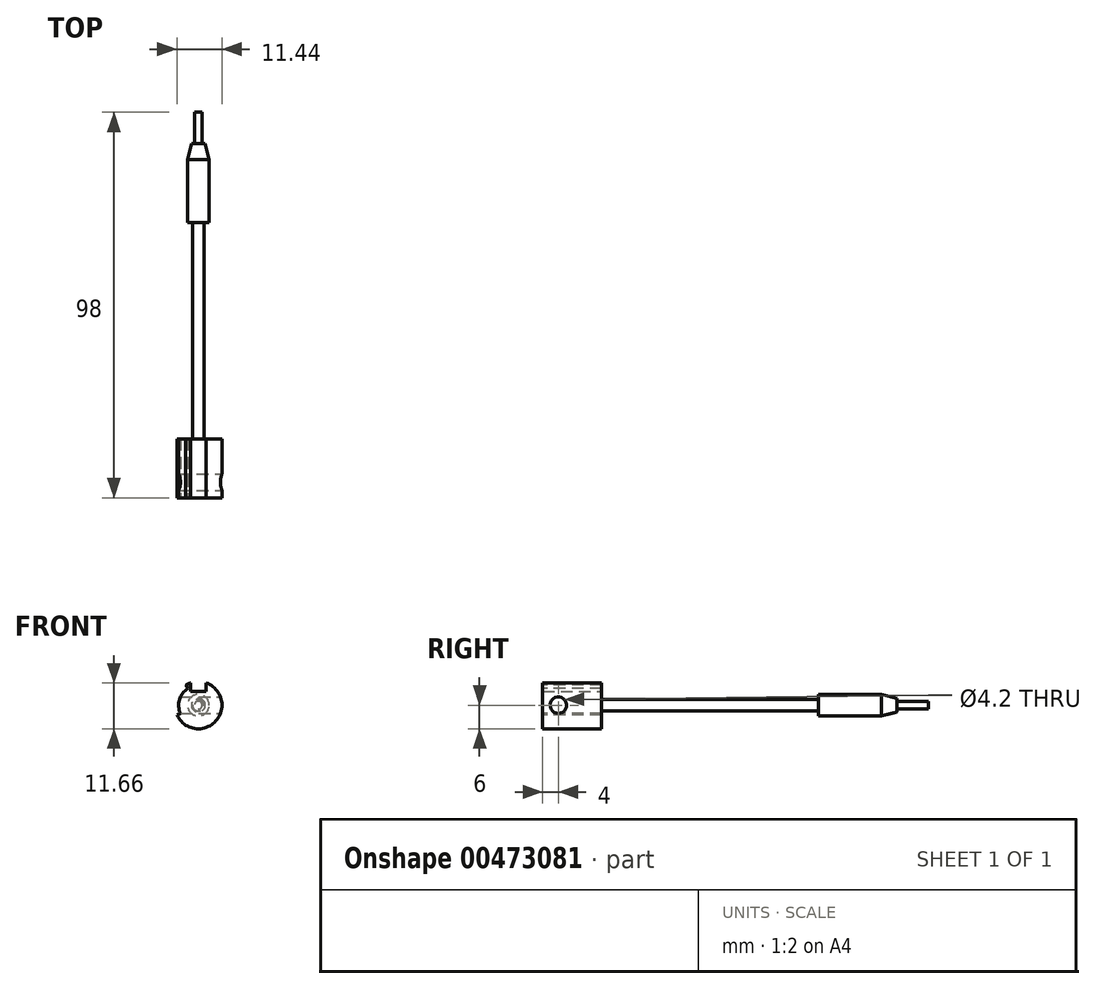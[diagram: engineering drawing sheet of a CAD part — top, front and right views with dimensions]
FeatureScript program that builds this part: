
annotation { "Feature Type Name" : "Feature", "Feature Type Description" : "" }
export const myFeature = defineFeature(function(context is Context, id is Id, definition is map)
    precondition{}
    {
        {
            var Q0;
            Q0=qCreatedBy(makeId("Front.planeOp"),FACE);
            var sketch = newSketch(context, id + "F0", { "sketchPlane" : qUnion([Q0])});
            skCircle(sketch, "E0", {"center": v(0, 0) * mm, "radius": 1 * mm});
            skSolve(sketch);
        }
        {
            var Q0;
            Q0=qSketchRegion(id+"F0",true);
            extrude(context, id + "F1", {"entities" : qUnion([Q0]), "oppositeDirection" : true, "depth" : 8 * mm});
        }
        {
            var Q0;
            Q0=makeQuery(id+"F1.opExtrude","CAP_FACE",FACE,{"disambiguationData":[OSD([sQuery(id+"F0.wireOp",EDGE,"E0")])],"isStart":true});
            var sketch = newSketch(context, id + "F2", { "sketchPlane" : qUnion([Q0])});
            skCircle(sketch, "E1", {"center": v(0, 0) * mm, "radius": 2.75 * mm});
            skSolve(sketch);
        }
        {
            var Q0;
            Q0=qSketchRegion(id+"F2",true);
            extrude(context, id + "F3", {"entities" : qUnion([Q0]), "operationType" : NewBodyOperationType.ADD, "depth" : 80 * mm});
        }
        {
            var Q0;
            Q0=makeQuery(id+"F3.opExtrude","CAP_EDGE",EDGE,{"disambiguationData":[OSD([sQuery(id+"F2.wireOp",EDGE,"E1")])],"isStart":true});
            chamfer(context, id + "F4", {"entities" : qUnion([Q0]), "chamferType" : ChamferType.TWO_OFFSETS, "width1" : 4 * mm, "oppositeDirection" : false, "width2" : 1 * mm, "tangentPropagation" : true});
        }
        {
            var Q0;
            Q0=makeQuery(id+"F3.opExtrude","CAP_FACE",FACE,{"disambiguationData":[OSD([sQuery(id+"F2.wireOp",EDGE,"E1")])],"isStart":false});
            var sketch = newSketch(context, id + "F5", { "sketchPlane" : qUnion([Q0])});
            skCircle(sketch, "E2", {"center": v(0, 0) * mm, "radius": 6 * mm});
            skSolve(sketch);
        }
        {
            var Q0;
            Q0=makeQuery(id+"F5.imprint","IMPRINT",FACE,{"disambiguationData":[TD([[makeQuery(id+"F5.imprint","IMPRINT",EDGE,{"derivedFrom":sQuery(id+"F5.wireOp",EDGE,"E2")}),1.0]])]});
            extrude(context, id + "F6", {"entities" : qUnion([Q0]), "operationType" : NewBodyOperationType.ADD, "oppositeDirection" : true, "depth" : 5 * mm});
        }
        {
            var Q0;
            Q0=makeQuery(id+"F6.boolean.opBoolean","MERGE",FACE,{"derivedFrom":[makeQuery(id+"F3.opExtrude","CAP_FACE",FACE,{"disambiguationData":[OSD([sQuery(id+"F2.wireOp",EDGE,"E1")])],"isStart":false}),makeQuery(id+"F6.opExtrude","CAP_FACE",FACE,{"disambiguationData":[OSD([sQuery(id+"F12.wireOp",EDGE,"E3"),sQuery(id+"F5.wireOp",EDGE,"E2")])],"isStart":true})]});
            extrude(context, id + "F7", {"entities" : qUnion([Q0]), "operationType" : NewBodyOperationType.ADD, "depth" : 10 * mm});
        }
        {
            var Q0;
            Q0=qCreatedBy(makeId("Right.planeOp"),FACE);
            cPlane(context, id + "F8", {"entities" : qUnion([Q0]), "cplaneType" : CPlaneType.OFFSET, "offset" : 6 * mm, "width" : 150 * mm, "height" : 150 * mm});
        }
        {
            var Q0;
            Q0=qCreatedBy(makeId("Top.planeOp"),FACE);
            cPlane(context, id + "F9", {"entities" : qUnion([Q0]), "cplaneType" : CPlaneType.OFFSET, "offset" : 6 * mm, "width" : 150 * mm, "height" : 150 * mm});
        }
        {
            var Q0;
            Q0=qCreatedBy(id+"F9.planeOp",FACE);
            var Q1;
            Q1=makeQuery(id+"F7.opExtrude","CAP_EDGE",EDGE,{"disambiguationData":[OSD([sQuery(id+"F5.wireOp",EDGE,"E2")])],"isStart":false});
            cPlane(context, id + "F10", {"entities" : qUnion([Q0, Q1]), "cplaneType" : CPlaneType.LINE_ANGLE, "offset" : 25 * mm, "angle" : 45 * degree, "width" : 150 * mm, "height" : 150 * mm});
        }
        {
            var Q0;
            Q0=qCreatedBy(id+"F10.planeOp",FACE);
            cPlane(context, id + "F11", {"entities" : qUnion([Q0]), "cplaneType" : CPlaneType.OFFSET, "offset" : 3.5 * mm, "width" : 150 * mm, "height" : 150 * mm});
        }
        {
            var Q0;
            Q0=makeQuery(id+"F6.opExtrude","CAP_FACE",FACE,{"disambiguationData":[OSD([sQuery(id+"F2.wireOp",EDGE,"E1"),sQuery(id+"F5.wireOp",EDGE,"E2")])],"isStart":false});
            var sketch = newSketch(context, id + "F12", { "sketchPlane" : qUnion([Q0])});
            skCircle(sketch, "E3", {"center": v(0, 0) * mm, "radius": 1.5 * mm});
            skCircle(sketch, "E4", {"center": v(0, 0) * mm, "radius": 2.75 * mm});
            skSolve(sketch);
        }
        {
            var Q0;
            Q0=makeQuery(id+"F12.imprint","IMPRINT",FACE,{"disambiguationData":[TD([[makeQuery(id+"F12.imprint","IMPRINT",EDGE,{"derivedFrom":sQuery(id+"F12.wireOp",EDGE,"E3")}),-1.0]])]});
            extrude(context, id + "F13", {"entities" : qUnion([Q0]), "operationType" : NewBodyOperationType.REMOVE, "depth" : 55 * mm});
        }
        {
            var Q0;
            Q0=qCreatedBy(id+"F8.planeOp",FACE);
            var sketch = newSketch(context, id + "F14", { "sketchPlane" : qUnion([Q0])});
            skPoint(sketch, "E5", {"position": v(-86, 0) * mm});
            skSolve(sketch);
        }
        {
            var Q0;
            Q0=sQuery(id+"F14.wireOp",VERTEX,"E5");
            var Q1;
            Q1=makeQuery(id+"F1.opExtrude","SWEPT_BODY",BODY,{"disambiguationData":[OSD([sQuery(id+"F0.wireOp",EDGE,"E0")])]});
            hole(context, id + "F15", {"style" : HoleStyle.SIMPLE, "endStyle" : HoleEndStyle.THROUGH, "standardTappedOrClearance" : lookupTablePath({ "standard" : "ISO", "engagement" : "75%", "pitch" : "0.8 mm", "size" : "M5", "type" : "Tapped" }), "standardBlindInLast" : lookupTablePath({ "standard" : "ISO", "engagement" : "75%", "pitch" : "0.8 mm", "size" : "M5", "type" : "Tapped" }), "holeDiameter" : 4.2 * mm, "showTappedDepth" : true, "isTappedThrough" : true, "tappedDepth" : 4 * mm, "tapClearance" : 3, "locations" : qUnion([Q0]), "scope" : qUnion([Q1]), "majorDiameter" : 5 * mm});
        }
        {
            var Q0;
            Q0=qCreatedBy(id+"F9.planeOp",FACE);
            var sketch = newSketch(context, id + "F16", { "sketchPlane" : qUnion([Q0])});
            skLineSegment(sketch, "E6.bottom", {"start": v(-2, -90) * mm, "end": v(2, -90) * mm});
            skLineSegment(sketch, "E6.top", {"start": v(-2, -75) * mm, "end": v(2, -75) * mm});
            skLineSegment(sketch, "E6.left", {"start": v(-2, -90) * mm, "end": v(-2, -75) * mm});
            skLineSegment(sketch, "E6.right", {"start": v(2, -90) * mm, "end": v(2, -75) * mm});
            skLineSegment(sketch, "E7", {"start": v(0, -90) * mm, "end": v(0, -75) * mm, "construction": true});
            skSolve(sketch);
        }
        {
            var Q0;
            Q0=qSketchRegion(id+"F16",true);
            extrude(context, id + "F17", {"entities" : qUnion([Q0]), "operationType" : NewBodyOperationType.REMOVE, "oppositeDirection" : true, "depth" : 2.5 * mm});
        }
        {
            var Q0;
            Q0=makeQuery(id+"F7.opExtrude","CAP_FACE",FACE,{"disambiguationData":[OSD([sQuery(id+"F2.wireOp",EDGE,"E1"),sQuery(id+"F5.wireOp",EDGE,"E2")])],"isStart":false});
            cPlane(context, id + "F18", {"entities" : qUnion([Q0]), "cplaneType" : CPlaneType.OFFSET, "offset" : 6.2 * mm, "oppositeDirection" : true, "width" : 150 * mm, "height" : 150 * mm});
        }
        {
            var Q0;
            Q0=qCreatedBy(makeId("Top.planeOp"),FACE);
            var Q1;
            {var subQ0=sQuery(id+"F5.wireOp",EDGE,"E2");Q1=makeQuery(id+"F17.boolean.opBoolean","SPLIT",EDGE,{"disambiguationData":[TD([makeQuery(id+"FctZoTc2OwpmKR8_1.boolean.opBoolean","COPY",FACE,{"derivedFrom":makeQuery(id+"FctZoTc2OwpmKR8_1.opExtrude","SWEPT_FACE",FACE,{"disambiguationData":[OSD([sQuery(id+"Fsz8UjHsgXwGy4J_1.wireOp",EDGE,"ASJJtbLU-RnPE-262p-RrrI-WQdVs2qlrqvg.left")])]})})])],"derivedFrom":makeQuery(id+"F7.opExtrude","CAP_EDGE",EDGE,{"disambiguationData":[OSD([subQ0])],"isStart":false})});}
            cPlane(context, id + "F19", {"entities" : qUnion([Q0, Q1]), "cplaneType" : CPlaneType.LINE_ANGLE, "offset" : 25 * mm, "angle" : 35 * degree, "oppositeDirection" : true, "width" : 150 * mm, "height" : 150 * mm});
        }
        {
            var Q0;
            Q0=qCreatedBy(id+"F19.planeOp",FACE);
            var Q1;
            Q1=makeQuery(id+"F3dtPzoqCMr70r0_1.boolean.opBoolean","MERGE",EDGE,{"derivedFrom":[makeQuery(id+"F17.boolean.opBoolean","COPY",EDGE,{"derivedFrom":makeQuery(id+"F17.opExtrude","CAP_EDGE",EDGE,{"disambiguationData":[OSD([sQuery(id+"F16.wireOp",EDGE,"E6.right")])],"isStart":false})}),makeQuery(id+"F3dtPzoqCMr70r0_1.opRevolve","CAP_EDGE",EDGE,{"disambiguationData":[OSD([sQuery(id+"FLutZ351tvMtZ2g_1.wireOp",EDGE,"eEcjrhR3-B4ge-PtRl-u11x-TswVySeL4WL9.top")]),OD(0.0)],"isStart":false})]});
            cPlane(context, id + "F20", {"entities" : qUnion([Q0, Q1]), "cplaneType" : CPlaneType.LINE_ANGLE, "offset" : 25 * mm, "angle" : 0 * degree, "width" : 150 * mm, "height" : 150 * mm});
        }
        {
            var Q0;
            Q0=qCreatedBy(id+"F20.planeOp",FACE);
            var Q1;
            Q1=makeQuery(id+"F3dtPzoqCMr70r0_1.boolean.opBoolean","MERGE",EDGE,{"derivedFrom":[makeQuery(id+"F17.boolean.opBoolean","COPY",EDGE,{"derivedFrom":makeQuery(id+"F17.opExtrude","CAP_EDGE",EDGE,{"disambiguationData":[OSD([sQuery(id+"F16.wireOp",EDGE,"E6.right")])],"isStart":false})}),makeQuery(id+"F3dtPzoqCMr70r0_1.opRevolve","CAP_EDGE",EDGE,{"disambiguationData":[OSD([sQuery(id+"FLutZ351tvMtZ2g_1.wireOp",EDGE,"eEcjrhR3-B4ge-PtRl-u11x-TswVySeL4WL9.top")]),OD(0.0)],"isStart":false})]});
            cPlane(context, id + "F21", {"entities" : qUnion([Q0, Q1]), "cplaneType" : CPlaneType.LINE_ANGLE, "offset" : 25 * mm, "angle" : 90 * degree, "width" : 150 * mm, "height" : 150 * mm});
        }
        {
            var Q0;
            Q0=qCreatedBy(id+"F20.planeOp",FACE);
            var sketch = newSketch(context, id + "F22", { "sketchPlane" : qUnion([Q0])});
            skPoint(sketch, "E8", {"position": v(-0.37, -83.8) * mm});
            skCircle(sketch, "E9", {"center": v(-0.37, -83.8) * mm, "radius": 1.25 * mm, "construction": true});
            skSolve(sketch);
        }
        {
            var Q0;
            Q0=makeQuery(id+"F7.opExtrude","CAP_FACE",FACE,{"disambiguationData":[OSD([sQuery(id+"F2.wireOp",EDGE,"E1"),sQuery(id+"F5.wireOp",EDGE,"E2")])],"isStart":false});
            var sketch = newSketch(context, id + "F23", { "sketchPlane" : qUnion([Q0])});
            skCircle(sketch, "E10", {"center": v(0, 0) * mm, "radius": 6 * mm});
            skCircle(sketch, "E11", {"center": v(0, 0) * mm, "radius": 5 * mm});
            skLineSegment(sketch, "E12", {"start": v(0, 0) * mm, "end": v(-5.44, -2.54) * mm});
            skLineSegment(sketch, "E13", {"start": v(0, 0) * mm, "end": v(-3.18, 5.09) * mm});
            skLineSegment(sketch, "E14", {"start": v(0, 0) * mm, "end": v(-6, 0) * mm, "construction": true});
            skSolve(sketch);
        }
        {
            var Q0;
            {var subQ0=sQuery(id+"F23.wireOp",EDGE,"E12");var subQ1=sQuery(id+"F23.wireOp",EDGE,"E10");var subQ2=makeQuery(id+"F23.imprint","INTERSECT",VERTEX,{"derivedFrom":[subQ1,subQ0]});Q0=makeQuery(id+"F23.imprint","IMPRINT",FACE,{"disambiguationData":[TD([[makeQuery(id+"F23.imprint","IMPRINT",EDGE,{"disambiguationData":[TD([[subQ2,1.0]])],"derivedFrom":subQ1}),1.0]])]});}
            extrude(context, id + "F24", {"entities" : qUnion([Q0]), "operationType" : NewBodyOperationType.REMOVE, "oppositeDirection" : true, "depth" : 15 * mm});
        }
    });
